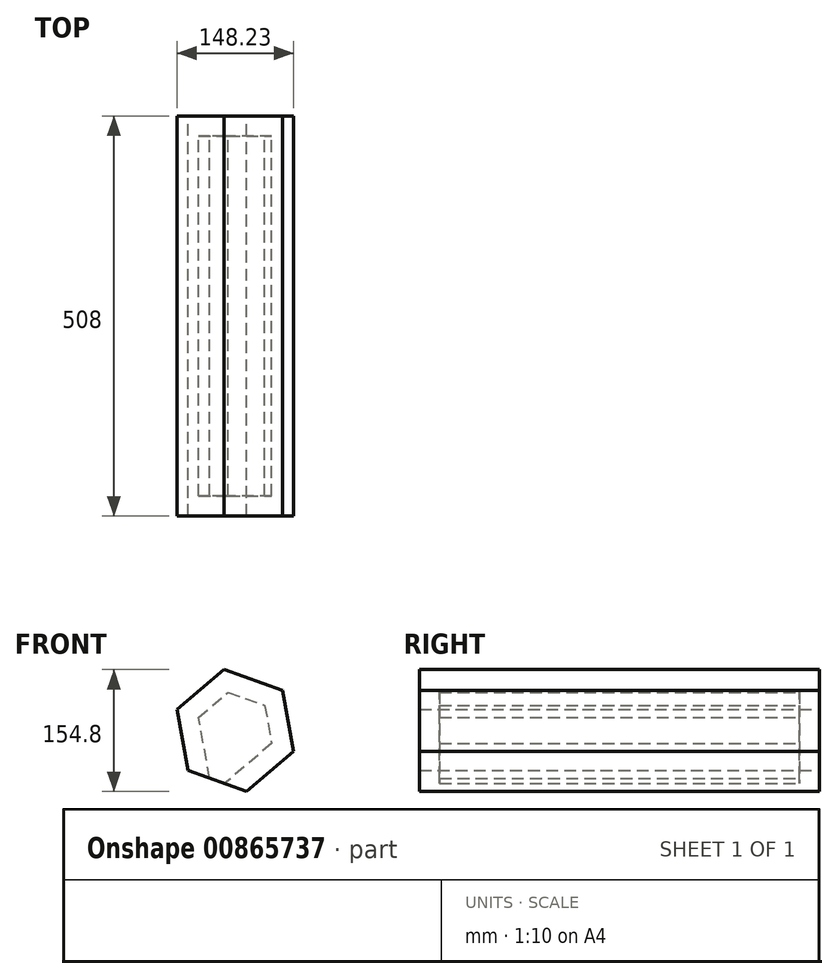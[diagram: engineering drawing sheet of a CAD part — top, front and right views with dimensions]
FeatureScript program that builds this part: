
annotation { "Feature Type Name" : "Feature", "Feature Type Description" : "" }
export const myFeature = defineFeature(function(context is Context, id is Id, definition is map)
    precondition{}
    {
        {
            var Q0;
            Q0=qCreatedBy(makeId("Front.planeOp"),FACE);
            var sketch = newSketch(context, id + "F0", { "sketchPlane" : qUnion([Q0])});
            skCircle(sketch, "E0.cCircle", {"center": v(15.4, 12.27) * mm, "radius": 68.15 * mm, "construction": true});
            skLineSegment(sketch, "E0.0", {"start": v(-44.56, -38.7) * mm, "end": v(-58.72, 38.7) * mm});
            skLineSegment(sketch, "E0.1", {"start": v(-58.72, 38.7) * mm, "end": v(1.23, 89.67) * mm});
            skLineSegment(sketch, "E0.2", {"start": v(1.23, 89.67) * mm, "end": v(75.34, 63.24) * mm});
            skLineSegment(sketch, "E0.3", {"start": v(75.34, 63.24) * mm, "end": v(89.51, -14.16) * mm});
            skLineSegment(sketch, "E0.4", {"start": v(89.51, -14.16) * mm, "end": v(29.56, -65.13) * mm});
            skLineSegment(sketch, "E0.5", {"start": v(29.56, -65.13) * mm, "end": v(-44.56, -38.7) * mm});
            skPoint(sketch, "E0.0.midPoint", {"position": v(-51.64, 0) * mm});
            skSolve(sketch);
        }
        {
            var Q0;
            Q0 = qSketchRegion(id + "F0", true);
            var Q1;
            Q1=makeQuery(id+"F0.imprint","IMPRINT",FACE,{"disambiguationData":[TD([[makeQuery(id+"F0.imprint","IMPRINT",EDGE,{"derivedFrom":sQuery(id+"F0.wireOp",EDGE,"E0.0")}),-1.0]])]});
            extrude(context, id + "F1", {"entities" : qUnion([Q0, Q1]), "depth" : 508 * mm, "offsetDistance" : 25.4 * mm});
        }
        {
            var Q0;
            Q0=makeQuery(id+"F1.opExtrude","SWEPT_FACE",FACE,{"disambiguationData":[OSD([sQuery(id+"F0.wireOp",EDGE,"E0.5")])]});
            shell(context, id + "F2", {"entities" : qUnion([Q0]), "thickness" : 25.4 * mm});
        }
    });
